# Revit family: Accessory-Accessory Kit-KOHLER-OCCASION-K-EX27077T
name_source: partatom
category: Specialty Equipment
units: mm (PartAtom-declared; Revit-internal decimal feet)

## family parameters
Cut with Voids When Loaded = No
Host = Face
OmniClass Number = 23.31.25.00
OmniClass Title = Toilet and Bath Specialties
Part Type = Normal
Room Calculation Point = No
Round Connector Dimension = Use Diameter
Shared = No

## types (2) — shared parameters
ADA Compliant = No
Assembly Code = C1030200
Date Modified = 01/30/2024
Default Elevation = 42"
Description = Counter Top Accessory Kit
Height = 9 1/16"
Length = 9 15/16"
Manufacturer = Kohler Co.
Master Format 2014 = 10 28 00
Master Format 2014 Name = Toilet, Bath, and Laundry Accessories
Material = Premium Metal Construction
Product Documentation Link = https://files.kohler.com.cn
Product Name = OCCASION
URL = http://www.kohler.com.cn
WaterSense Certified = No
Width = 4 13/16"

## per-type parameters (varying)
| type | Finish | Model | Type |
| BRD-Brushed Rose Gold | KOHLER-Metal-BRD-Brushed_Rose_Gold | K-EX27077T-BRD | 1 |
| BRT-Brushed Titanium | KOHLER-Metal-BRT-Brushed_Titanium | K-EX27077T-BRT | 2 |

## geometry (parser evidence)
native form markers: Sweep x10
no freeform markers — native parametric forms only
